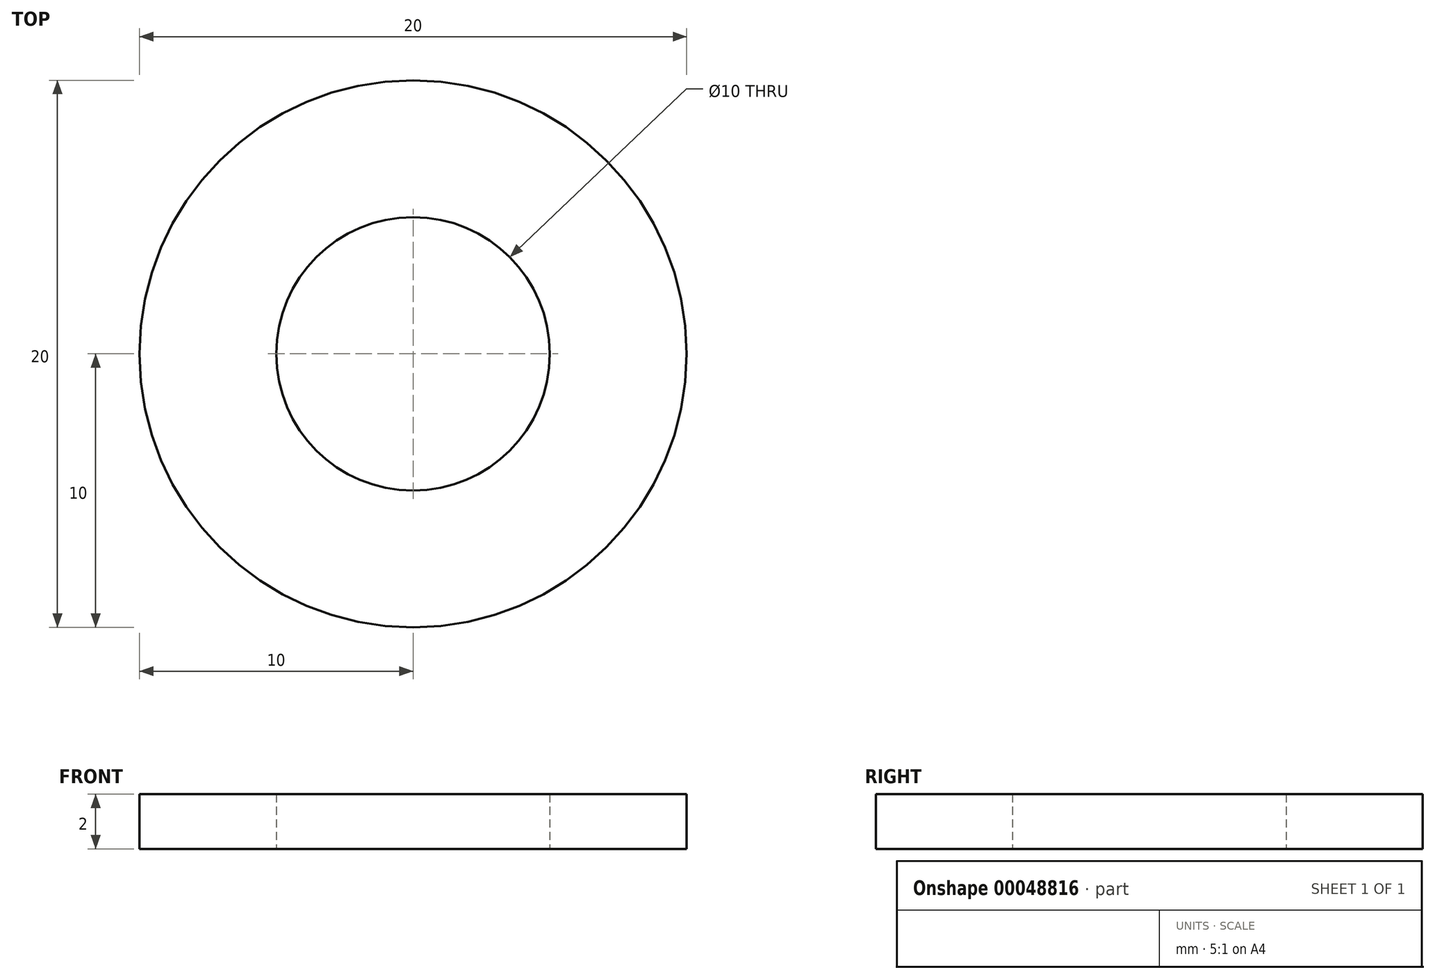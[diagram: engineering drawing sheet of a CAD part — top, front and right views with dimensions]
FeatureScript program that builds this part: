
annotation { "Feature Type Name" : "Feature", "Feature Type Description" : "" }
export const myFeature = defineFeature(function(context is Context, id is Id, definition is map)
    precondition{}
    {
        {
            var Q0;
            Q0=qCreatedBy(makeId("Top.planeOp"),FACE);
            var sketch = newSketch(context, id + "F0", { "sketchPlane" : qUnion([Q0])});
            skCircle(sketch, "E0", {"center": v(0, 0) * mm, "radius": 5 * mm});
            skCircle(sketch, "E1", {"center": v(0, 0) * mm, "radius": 10 * mm});
            skSolve(sketch);
        }
        {
            var Q0;
            Q0=makeQuery(id+"F0.imprint","IMPRINT",FACE,{"disambiguationData":[TD([[makeQuery(id+"F0.imprint","IMPRINT",EDGE,{"derivedFrom":sQuery(id+"F0.wireOp",EDGE,"E0")}),-1.0]])]});
            extrude(context, id + "F1", {"entities" : qUnion([Q0]), "depth" : 2 * mm});
        }
    });
